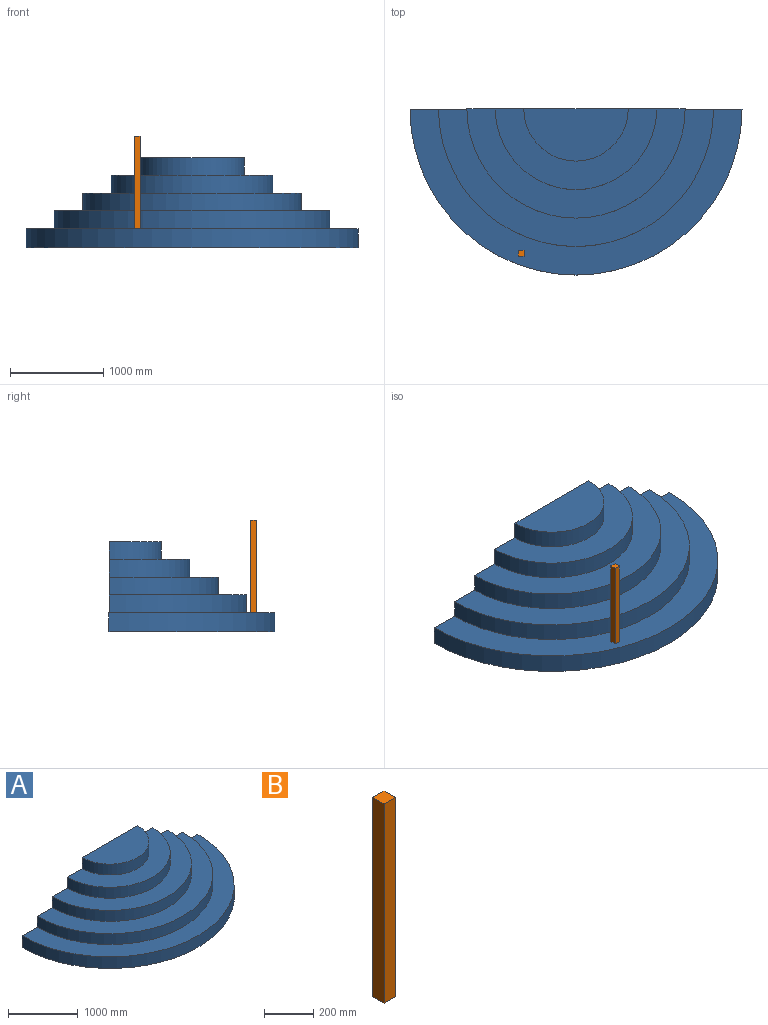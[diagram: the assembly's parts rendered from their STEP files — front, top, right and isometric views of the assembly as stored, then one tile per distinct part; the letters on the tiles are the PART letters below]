
ASSEMBLY  parts=2 mates=1
PART A: 12 faces, bbox 3556x1778x965.2 mm
  f0: plane 3556x1778mm, normal (0,0,-1), area 4965733.3mm2, adj f10,f11
  f1: plane 1117.6x558.8mm, normal (0,0,1), area 490492.8mm2, adj f2,f11
  f2: cylinder r=558.8mm len=1117.6mm, axis (0,0,1), area 334426.9mm2, adj f1,f3,f11
  f3: plane 1727.2x863.6mm, normal (0,0,1), area 681014.9mm2, adj f2,f4,f11
  f4: cylinder r=863.6mm len=1727.2mm, axis (0,0,1), area 516841.6mm2, adj f3,f5,f11
  f5: plane 2336.8x1168.4mm, normal (0,0,1), area 972878.4mm2, adj f4,f6,f11
  f6: cylinder r=1168.4mm len=2336.8mm, axis (0,0,1), area 699256.3mm2, adj f5,f7,f11
  f7: plane 2946.4x1473.2mm, normal (0,0,1), area 1264741.9mm2, adj f6,f8,f11
  f8: cylinder r=1473.2mm len=2946.4mm, axis (0,0,1), area 881671mm2, adj f7,f9,f11
  f9: plane 3556x1778mm, normal (0,0,1), area 1556605.4mm2, adj f8,f10,f11
  f10: cylinder r=1778mm len=3556mm, axis (0,0,1), area 1135024.8mm2, adj f0,f9,f11
  f11: plane 3556x965.2mm, normal (0,1,0), area 2270963.2mm2, adj f0,f1,f2,f3,f4,f5,f6,f7
PART B: 6 faces, bbox 63.5x63.5x990.6 mm
  f0: plane 990.6x63.5mm, normal (0,1,0), area 62903.1mm2, adj f1,f3,f4,f5
  f1: plane 990.6x63.5mm, normal (-1,0,0), area 62903.1mm2, adj f0,f2,f4,f5
  f2: plane 990.6x63.5mm, normal (0,-1,0), area 62903.1mm2, adj f1,f3,f4,f5
  f3: plane 990.6x63.5mm, normal (1,0,0), area 62903.1mm2, adj f0,f2,f4,f5
  f4: plane 63.5x63.5mm, normal (0,0,1), area 4032.3mm2, adj f0,f1,f2,f3
  f5: plane 63.5x63.5mm, normal (0,0,-1), area 4032.3mm2, adj f0,f1,f2,f3
PLACE A t=(0,0,-279.67)mm
PLACE B t=(-620.02,262.95,-76.47)mm
MATE planar B.f5 <-> A.f9  axis (0,0,-1) through (-588.27,231.2,-76.47)mm
